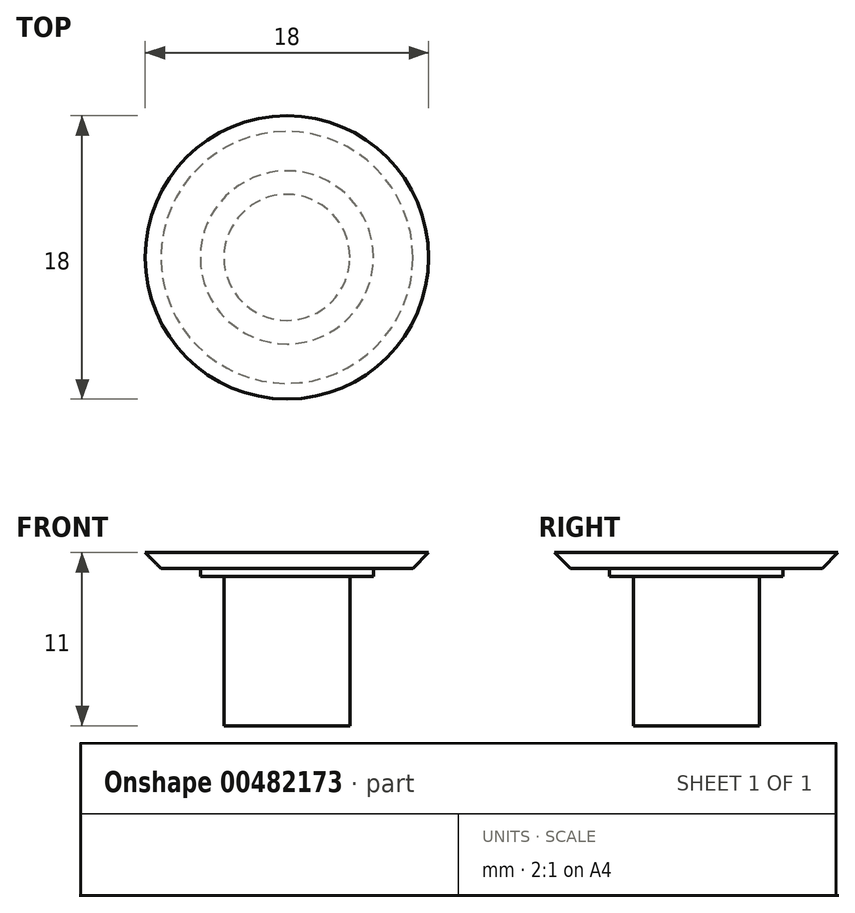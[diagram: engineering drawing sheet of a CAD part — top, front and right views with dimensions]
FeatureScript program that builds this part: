
annotation { "Feature Type Name" : "Feature", "Feature Type Description" : "" }
export const myFeature = defineFeature(function(context is Context, id is Id, definition is map)
    precondition{}
    {
        {
            var Q0;
            Q0=qCreatedBy(makeId("Front.planeOp"),FACE);
            var sketch = newSketch(context, id + "F0", { "sketchPlane" : qUnion([Q0])});
            skLineSegment(sketch, "E0.bottom", {"start": v(0, 0) * mm, "end": v(-4, 0) * mm});
            skLineSegment(sketch, "E0.top", {"start": v(0, 10) * mm, "end": v(-4, 10) * mm});
            skLineSegment(sketch, "E0.left", {"start": v(0, 0) * mm, "end": v(0, 10) * mm});
            skLineSegment(sketch, "E0.right", {"start": v(-4, 0) * mm, "end": v(-4, 10) * mm});
            skLineSegment(sketch, "E1.bottom", {"start": v(-4, 9) * mm, "end": v(-11, 9) * mm});
            skLineSegment(sketch, "E1.top", {"start": v(-4, 10) * mm, "end": v(-11, 10) * mm});
            skLineSegment(sketch, "E1.left", {"start": v(-4, 9) * mm, "end": v(-4, 10) * mm});
            skLineSegment(sketch, "E1.right", {"start": v(-11, 9) * mm, "end": v(-11, 10) * mm});
            skLineSegment(sketch, "E2", {"start": v(-5.5, 9) * mm, "end": v(-5.5, 8.5) * mm});
            skLineSegment(sketch, "E3", {"start": v(-5.5, 8.5) * mm, "end": v(-4, 8.5) * mm});
            skLineSegment(sketch, "E4.bottom", {"start": v(-4, 0) * mm, "end": v(0, 0) * mm});
            skLineSegment(sketch, "E4.top", {"start": v(-4, -1) * mm, "end": v(0, -1) * mm});
            skLineSegment(sketch, "E4.left", {"start": v(-4, 0) * mm, "end": v(-4, -1) * mm});
            skLineSegment(sketch, "E4.right", {"start": v(0, 0) * mm, "end": v(0, -1) * mm});
            skSolve(sketch);
        }
        {
            var Q0;
            Q0 = qSketchRegion(id + "F0", true);
            var Q1;
            Q1=sQuery(id+"F0.wireOp",EDGE,"E0.left");
            revolve(context, id + "F1", {"entities" : qUnion([Q0]), "axis" : qUnion([Q1]), "revolveType" : RevolveType.FULL});
        }
        {
            var Q0;
            Q0=makeQuery(id+"F1.opRevolve","SWEPT_EDGE",EDGE,{"disambiguationData":[OSD([sQuery(id+"F0.wireOp",EDGE,"E1.bottom"),sQuery(id+"F0.wireOp",EDGE,"E1.right")])]});
            chamfer(context, id + "F2", {"entities" : qUnion([Q0]), "width" : 3 * mm, "tangentPropagation" : true});
        }
    });
